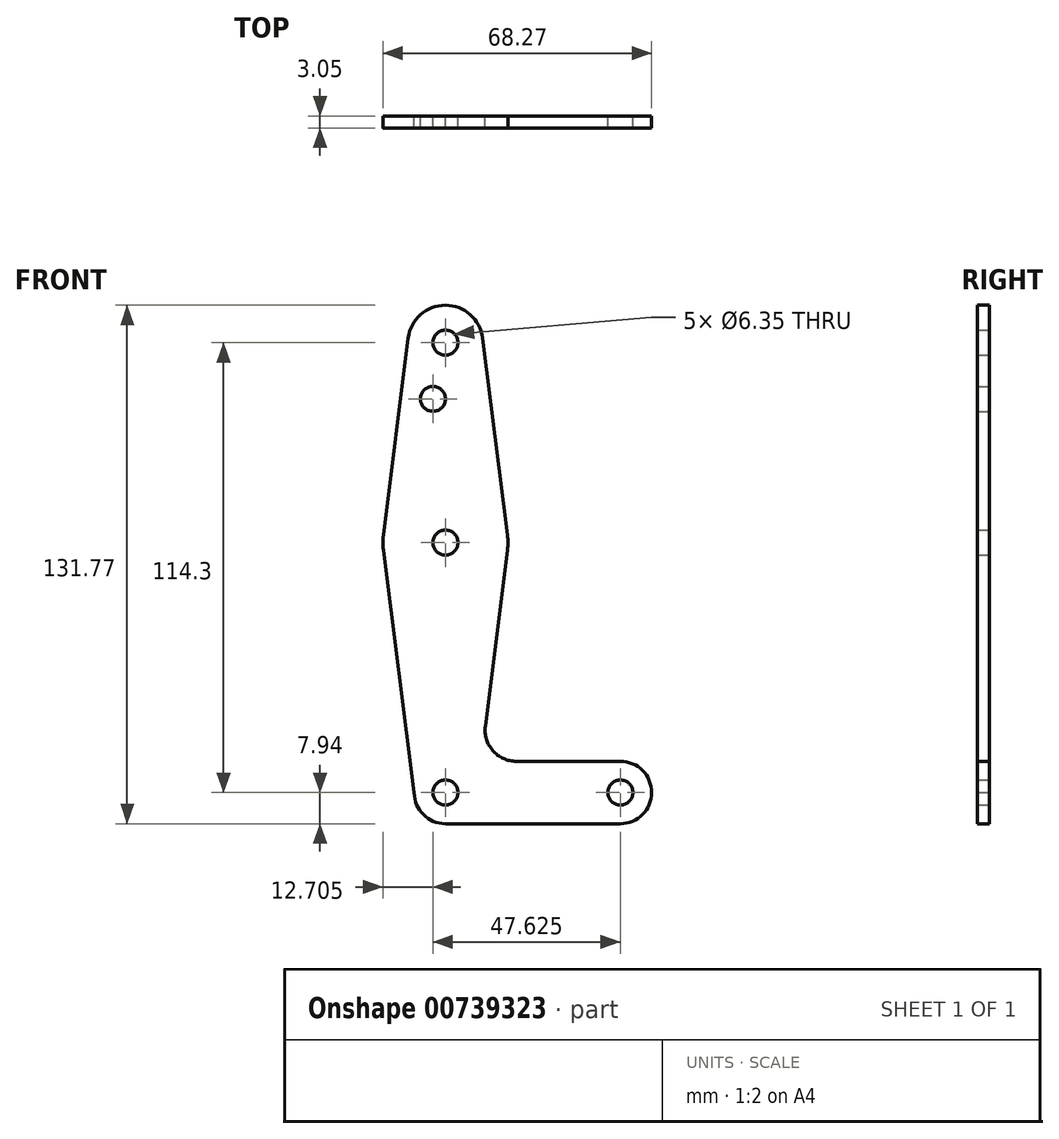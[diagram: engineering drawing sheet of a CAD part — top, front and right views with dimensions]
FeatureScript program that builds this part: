
annotation { "Feature Type Name" : "Feature", "Feature Type Description" : "" }
export const myFeature = defineFeature(function(context is Context, id is Id, definition is map)
    precondition{}
    {
        {
            var Q0;
            Q0=qCreatedBy(makeId("Front.planeOp"),FACE);
            var sketch = newSketch(context, id + "F0", { "sketchPlane" : qUnion([Q0])});
            skLineSegment(sketch, "E0", {"start": v(0, 0) * mm, "end": v(0, 114.3) * mm});
            skLineSegment(sketch, "E1", {"start": v(0, 0) * mm, "end": v(44.45, 0) * mm});
            skCircle(sketch, "E2", {"center": v(0, 114.3) * mm, "radius": 9.53 * mm});
            skCircle(sketch, "E3", {"center": v(0, 63.5) * mm, "radius": 15.88 * mm});
            skCircle(sketch, "E4", {"center": v(0, 0) * mm, "radius": 7.94 * mm});
            skCircle(sketch, "E5", {"center": v(44.45, 0) * mm, "radius": 7.94 * mm});
            skLineSegment(sketch, "E6", {"start": v(-9.45, 115.5) * mm, "end": v(-15.75, 65.48) * mm});
            skLineSegment(sketch, "E7", {"start": v(9.45, 115.5) * mm, "end": v(15.75, 65.48) * mm});
            skLineSegment(sketch, "E8", {"start": v(-15.75, 61.5) * mm, "end": v(-7.94, 0) * mm});
            skLineSegment(sketch, "E9", {"start": v(15.75, 61.52) * mm, "end": v(10.13, 16.88) * mm});
            skLineSegment(sketch, "E10", {"start": v(18.01, 7.94) * mm, "end": v(44.45, 7.94) * mm});
            skLineSegment(sketch, "E11", {"start": v(0, -7.94) * mm, "end": v(44.45, -7.94) * mm});
            skCircle(sketch, "E12", {"center": v(-3.18, 100.03) * mm, "radius": 3.18 * mm});
            skCircle(sketch, "E13", {"center": v(0, 114.3) * mm, "radius": 3.18 * mm});
            skCircle(sketch, "E14", {"center": v(0, 63.5) * mm, "radius": 3.18 * mm});
            skCircle(sketch, "E15", {"center": v(0, 0) * mm, "radius": 3.18 * mm});
            skCircle(sketch, "E16", {"center": v(44.45, 0) * mm, "radius": 3.17 * mm});
            skArc(sketch, "E17.filletArc", {"start": v(10.13, 16.88) * mm, "mid": v(12.05, 10.63) * mm, "end": v(18.01, 7.94) * mm});
            skSolve(sketch);
        }
        {
            var Q0;
            Q0 = qSketchRegion(id + "F0", true);
            var Q1;
            {var subQ0=sQuery(id+"F0.wireOp",EDGE,"E15");var subQ1=sQuery(id+"F0.wireOp",EDGE,"E0");var subQ2=makeQuery(id+"F0.imprint","INTERSECT",VERTEX,{"derivedFrom":[subQ1,subQ0]});Q1=makeQuery(id+"F0.imprint","IMPRINT",FACE,{"disambiguationData":[TD([[makeQuery(id+"F0.imprint","IMPRINT",EDGE,{"disambiguationData":[TD([[subQ2,-1.0]])],"derivedFrom":subQ1}),-1.0]])]});}
            extrude(context, id + "F1", {"entities" : qUnion([Q0, Q1]), "depth" : 3.05 * mm, "offsetDistance" : 25.4 * mm});
        }
    });
